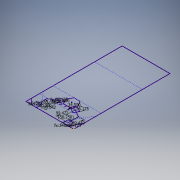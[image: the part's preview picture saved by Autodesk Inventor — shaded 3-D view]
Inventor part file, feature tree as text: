
AUTODESK INVENTOR PART (.ipt)
format: ipt  version: 2017 (Build 210142000, 142)  size: 145,920 bytes
history: native  units: in
note: dims shown in document units (in); Inventor stores cm internally (conversion verified against a paired STEP export)
features: other x2, sketch x1
ambient origin geometry x8: Origin, YZ Plane, XZ Plane, XY Plane, X Axis, Y Axis, Z Axis, Center Point
feature tree (3):
  other  "FieldSketch"
  other  "WallToBoilerPegPath"
  sketch  "Sketch3"  dims[d0=652.0in d2=36.375in d3=37.0in d4=37.75in d5=67.375in d6=71.0in d7=113.892in d9=162.0in d11=3.375in d12=2.5in d13=10.63in d14=3.375in d15=2.5in d16=2.5in d17=3.375in d18=10.63in d19=10.63in d20=324.0in d21=93.18in d22=120.0deg d23=120.0deg d24=184.8in d25=465.0in d26=52.0in d27=42.0in d28=36.125in d29=34.5in d30=36.125in d31=34.5in d32=50.0in d35=52.0in d36=99.0416in d37=36.125in d38=34.5in d39=34.5in d40=36.125in d41=70.4097in d42=99.4216in d43=50.2501in]
